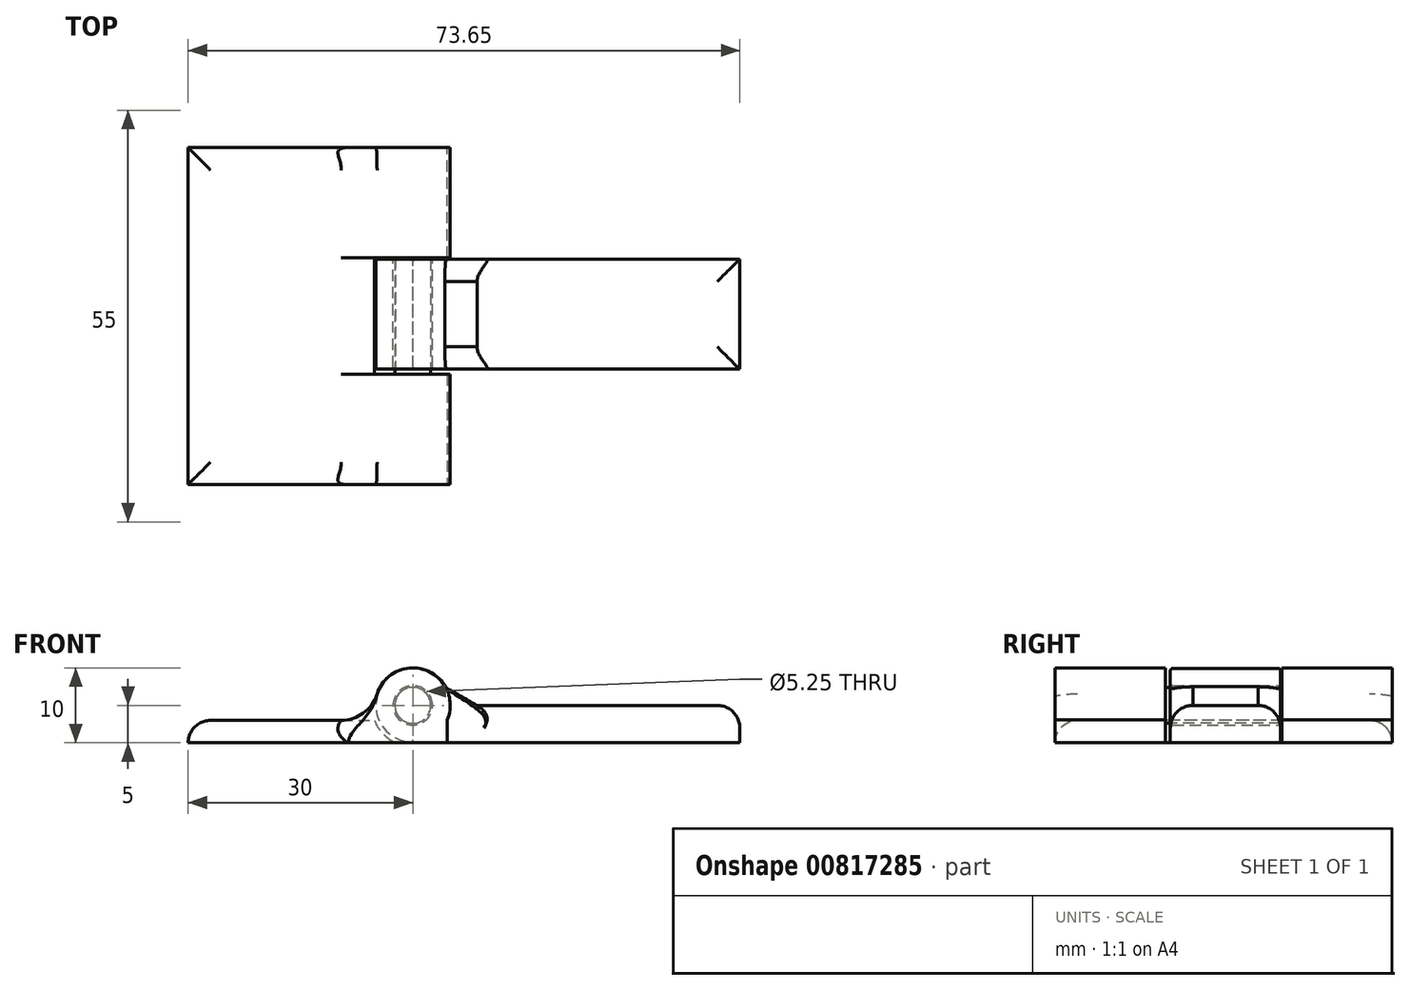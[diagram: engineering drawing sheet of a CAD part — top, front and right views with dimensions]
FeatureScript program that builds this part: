
annotation { "Feature Type Name" : "Feature", "Feature Type Description" : "" }
export const myFeature = defineFeature(function(context is Context, id is Id, definition is map)
    precondition{}
    {
        {
            var Q0;
            Q0=qCreatedBy(makeId("Top.planeOp"),FACE);
            var sketch = newSketch(context, id + "F0", { "sketchPlane" : qUnion([Q0])});
            skLineSegment(sketch, "E0.bottom", {"start": v(0, 0) * mm, "end": v(-30, 0) * mm});
            skLineSegment(sketch, "E0.top", {"start": v(0, -45) * mm, "end": v(-30, -45) * mm});
            skLineSegment(sketch, "E0.left", {"start": v(0, 0) * mm, "end": v(0, -45) * mm});
            skLineSegment(sketch, "E0.right", {"start": v(-30, 0) * mm, "end": v(-30, -45) * mm});
            skSolve(sketch);
        }
        {
            var Q0;
            Q0 = qSketchRegion(id + "F0", true);
            extrude(context, id + "F1", {"entities" : qUnion([Q0]), "depth" : 3 * mm, "offsetDistance" : 25 * mm});
        }
        {
            var Q0;
            Q0=makeQuery(id+"F1.opExtrude","SWEPT_FACE",FACE,{"disambiguationData":[OSD([sQuery(id+"F0.wireOp",EDGE,"E0.top")])]});
            var sketch = newSketch(context, id + "F2", { "sketchPlane" : qUnion([Q0])});
            skCircle(sketch, "E1", {"center": v(0, 5) * mm, "radius": 5 * mm});
            skLineSegment(sketch, "E2.bottom", {"start": v(0, 0) * mm, "end": v(4.6, 0) * mm});
            skLineSegment(sketch, "E2.top", {"start": v(0, 3.04) * mm, "end": v(4.6, 3.04) * mm});
            skLineSegment(sketch, "E2.left", {"start": v(0, 0) * mm, "end": v(0, 3.04) * mm});
            skLineSegment(sketch, "E2.right", {"start": v(4.6, 0) * mm, "end": v(4.6, 3.04) * mm});
            skSolve(sketch);
        }
        {
            var Q0;
            Q0 = qSketchRegion(id + "F2", true);
            extrude(context, id + "F3", {"entities" : qUnion([Q0]), "operationType" : NewBodyOperationType.ADD, "oppositeDirection" : true, "depth" : 14.7 * mm, "offsetDistance" : 25 * mm});
        }
        {
            var Q0;
            Q0=makeQuery(id+"F1.opExtrude","SWEPT_FACE",FACE,{"disambiguationData":[OSD([sQuery(id+"F0.wireOp",EDGE,"E0.bottom")])]});
            var sketch = newSketch(context, id + "F4", { "sketchPlane" : qUnion([Q0])});
            skCircle(sketch, "E3", {"center": v(0, 5) * mm, "radius": 5 * mm});
            skLineSegment(sketch, "E4.bottom", {"start": v(0, 0) * mm, "end": v(-4.6, 0) * mm});
            skLineSegment(sketch, "E4.top", {"start": v(0, 3.04) * mm, "end": v(-4.6, 3.04) * mm});
            skLineSegment(sketch, "E4.left", {"start": v(0, 0) * mm, "end": v(0, 3.04) * mm});
            skLineSegment(sketch, "E4.right", {"start": v(-4.6, 0) * mm, "end": v(-4.6, 3.04) * mm});
            skSolve(sketch);
        }
        {
            var Q0;
            Q0 = qSketchRegion(id + "F4", true);
            extrude(context, id + "F5", {"entities" : qUnion([Q0]), "operationType" : NewBodyOperationType.ADD, "oppositeDirection" : true, "depth" : 14.7 * mm, "offsetDistance" : 25 * mm});
        }
        {
            var Q0;
            Q0=makeQuery(id+"F3.opExtrude","CAP_FACE",FACE,{"disambiguationData":[OSD([sQuery(id+"F2.wireOp",EDGE,"E1")])],"isStart":false});
            var sketch = newSketch(context, id + "F6", { "sketchPlane" : qUnion([Q0])});
            skCircle(sketch, "E5", {"center": v(0, 5) * mm, "radius": 5.5 * mm});
            skSolve(sketch);
        }
        {
            var Q0;
            Q0 = qSketchRegion(id + "F6", true);
            var Q1;
            Q1=makeQuery(id+"F5.opExtrude","CAP_FACE",FACE,{"disambiguationData":[OSD([sQuery(id+"F4.wireOp",EDGE,"E3")])],"isStart":false});
            extrude(context, id + "F7", {"entities" : qUnion([Q0]), "operationType" : NewBodyOperationType.REMOVE, "endBound" : BoundingType.UP_TO_SURFACE, "depth" : 25 * mm, "endBoundEntityFace" : qUnion([Q1]), "offsetDistance" : 25 * mm});
        }
        {
            var Q0;
            Q0=makeQuery(id+"F3.boolean.opBoolean","MERGE",FACE,{"derivedFrom":[makeQuery(id+"F1.opExtrude","SWEPT_FACE",FACE,{"disambiguationData":[OSD([sQuery(id+"F0.wireOp",EDGE,"E0.top")])]}),makeQuery(id+"F3.opExtrude","CAP_FACE",FACE,{"disambiguationData":[OSD([sQuery(id+"F2.wireOp",EDGE,"E1")])],"isStart":true})]});
            var sketch = newSketch(context, id + "F8", { "sketchPlane" : qUnion([Q0])});
            skCircle(sketch, "E6", {"center": v(0, 5) * mm, "radius": 2.4 * mm});
            skSolve(sketch);
        }
        {
            var Q0;
            Q0 = qSketchRegion(id + "F8", true);
            var Q1;
            Q1=makeQuery(id+"F5.opExtrude","CAP_FACE",FACE,{"disambiguationData":[OSD([sQuery(id+"F4.wireOp",EDGE,"E3")])],"isStart":false});
            extrude(context, id + "F9", {"entities" : qUnion([Q0]), "operationType" : NewBodyOperationType.ADD, "endBound" : BoundingType.UP_TO_SURFACE, "oppositeDirection" : true, "depth" : 25 * mm, "endBoundEntityFace" : qUnion([Q1]), "offsetDistance" : 25 * mm});
        }
        {
            var Q0;
            {var subQ0=sQuery(id+"F4.wireOp",EDGE,"E4.right");var subQ1=sQuery(id+"F4.wireOp",EDGE,"E4.bottom");var subQ2=sQuery(id+"F4.wireOp",EDGE,"E3");Q0=makeQuery(id+"F7.boolean.opBoolean","MERGE",FACE,{"derivedFrom":[makeQuery(id+"F5.opExtrude","CAP_FACE",FACE,{"disambiguationData":[OSD([subQ2,subQ1,subQ0])],"isStart":false}),makeQuery(id+"F7.opExtrude","CAP_FACE",FACE,{"disambiguationData":[OSD([subQ2,subQ1,subQ0])],"isStart":false})]});}
            cPlane(context, id + "F10", {"entities" : qUnion([Q0]), "cplaneType" : CPlaneType.OFFSET, "offset" : .2 * mm, "width" : 150 * mm, "height" : 150 * mm});
        }
        {
            var Q0;
            Q0=qCreatedBy(id+"F10.planeOp",FACE);
            var sketch = newSketch(context, id + "F11", { "sketchPlane" : qUnion([Q0])});
            skCircle(sketch, "E7", {"center": v(0, 5) * mm, "radius": 2.62 * mm});
            skCircle(sketch, "E8", {"center": v(0, 5) * mm, "radius": 4.92 * mm});
            skLineSegment(sketch, "E9.bottom", {"start": v(3.65, 5) * mm, "end": v(43.65, 5) * mm});
            skLineSegment(sketch, "E9.top", {"start": v(3.65, 0) * mm, "end": v(43.65, 0) * mm});
            skLineSegment(sketch, "E9.left", {"start": v(3.65, 5) * mm, "end": v(3.65, 0) * mm});
            skLineSegment(sketch, "E9.right", {"start": v(43.65, 5) * mm, "end": v(43.65, 0) * mm});
            skLineSegment(sketch, "E10.bottom", {"start": v(3.65, 0) * mm, "end": v(0, 0) * mm});
            skLineSegment(sketch, "E10.top", {"start": v(3.65, 2.38) * mm, "end": v(0, 2.38) * mm});
            skLineSegment(sketch, "E10.left", {"start": v(3.65, 0) * mm, "end": v(3.65, 2.38) * mm});
            skLineSegment(sketch, "E10.right", {"start": v(0, 0) * mm, "end": v(0, 2.38) * mm});
            skSolve(sketch);
        }
        {
            var Q0;
            Q0 = qSketchRegion(id + "F11", true);
            extrude(context, id + "F12", {"entities" : qUnion([Q0]), "depth" : 14.7 * mm, "offsetDistance" : 25 * mm});
        }
        {
            var Q0;
            Q0=makeQuery(id+"F1.opExtrude","CAP_EDGE",EDGE,{"disambiguationData":[OSD([sQuery(id+"F0.wireOp",EDGE,"E0.bottom")])],"isStart":false});
            var Q1;
            Q1=makeQuery(id+"F1.opExtrude","CAP_EDGE",EDGE,{"disambiguationData":[OSD([sQuery(id+"F0.wireOp",EDGE,"E0.right")])],"isStart":false});
            var Q2;
            Q2=makeQuery(id+"F1.opExtrude","CAP_EDGE",EDGE,{"disambiguationData":[OSD([sQuery(id+"F0.wireOp",EDGE,"E0.top")])],"isStart":false});
            var Q3;
            Q3=makeQuery(id+"F12.opExtrude","CAP_EDGE",EDGE,{"disambiguationData":[OSD([sQuery(id+"F11.wireOp",EDGE,"E9.bottom")])],"isStart":false});
            var Q4;
            Q4=makeQuery(id+"F12.opExtrude","CAP_EDGE",EDGE,{"disambiguationData":[OSD([sQuery(id+"F11.wireOp",EDGE,"E9.bottom")])],"isStart":true});
            var Q5;
            Q5=makeQuery(id+"F12.opExtrude","SWEPT_EDGE",EDGE,{"disambiguationData":[OSD([sQuery(id+"F11.wireOp",EDGE,"E9.bottom"),sQuery(id+"F11.wireOp",EDGE,"E9.right")])]});
            fillet(context, id + "F13", {"entities" : qUnion([Q0, Q1, Q2, Q3, Q4, Q5]), "radius" : 3 * mm, "tangentPropagation" : true, "allowEdgeOverflow" : false});
        }
        {
            var Q0;
            Q0=makeQuery(id+"F12.opExtrude","SWEPT_EDGE",EDGE,{"disambiguationData":[OSD([sQuery(id+"F11.wireOp",EDGE,"E8"),sQuery(id+"F11.wireOp",EDGE,"E9.bottom")])]});
            chamfer(context, id + "F14", {"entities" : qUnion([Q0]), "width" : 5 * mm, "tangentPropagation" : true});
        }
        {
            var Q0;
            Q0=makeQuery(id+"F12.opExtrude","CAP_EDGE",EDGE,{"disambiguationData":[OSD([sQuery(id+"F11.wireOp",EDGE,"E7")])],"isStart":true});
            var Q1;
            {var subQ0=sQuery(id+"F4.wireOp",EDGE,"E4.right");var subQ1=sQuery(id+"F4.wireOp",EDGE,"E4.bottom");var subQ2=sQuery(id+"F4.wireOp",EDGE,"E3");Q1=makeQuery(id+"F9.opExtrude","TWEAK_EDGE",EDGE,{"derivedFrom":[makeQuery(id+"F7.boolean.opBoolean","MERGE",FACE,{"derivedFrom":[makeQuery(id+"F5.opExtrude","CAP_FACE",FACE,{"disambiguationData":[OSD([subQ2,subQ1,subQ0])],"isStart":false}),makeQuery(id+"F7.opExtrude","CAP_FACE",FACE,{"disambiguationData":[OSD([subQ2,subQ1,subQ0])],"isStart":false})]}),makeQuery(id+"F8.imprint","IMPRINT",EDGE,{"derivedFrom":sQuery(id+"F8.wireOp",EDGE,"E6")})]});}
            var Q2;
            Q2=makeQuery(id+"F12.opExtrude","CAP_EDGE",EDGE,{"disambiguationData":[OSD([sQuery(id+"F11.wireOp",EDGE,"E8")])],"isStart":true});
            var Q3;
            Q3=makeQuery(id+"F12.opExtrude","CAP_EDGE",EDGE,{"disambiguationData":[OSD([sQuery(id+"F11.wireOp",EDGE,"E8")])],"isStart":false});
            var Q4;
            Q4=makeQuery(id+"F9.boolean.opBoolean","INTERSECT",EDGE,{"derivedFrom":[makeQuery(id+"F7.boolean.opBoolean","MERGE",FACE,{"derivedFrom":[makeQuery(id+"F3.opExtrude","CAP_FACE",FACE,{"disambiguationData":[OSD([sQuery(id+"F2.wireOp",EDGE,"E1"),sQuery(id+"F2.wireOp",EDGE,"E2.bottom"),sQuery(id+"F2.wireOp",EDGE,"E2.right")])],"isStart":false}),makeQuery(id+"F7.opExtrude","CAP_FACE",FACE,{"disambiguationData":[OSD([sQuery(id+"F6.wireOp",EDGE,"E5")])],"isStart":true})]}),makeQuery(id+"F9.opExtrude","SWEPT_FACE",FACE,{"disambiguationData":[OSD([sQuery(id+"F8.wireOp",EDGE,"E6")])]})]});
            var Q5;
            Q5=makeQuery(id+"F12.opExtrude","CAP_EDGE",EDGE,{"disambiguationData":[OSD([sQuery(id+"F11.wireOp",EDGE,"E7")])],"isStart":false});
            fillet(context, id + "F15", {"entities" : qUnion([Q0, Q1, Q2, Q3, Q4, Q5]), "radius" : .3 * mm, "tangentPropagation" : true, "allowEdgeOverflow" : false});
        }
        {
            var Q0;
            Q0=makeQuery(id+"F5.boolean.opBoolean","INTERSECT",EDGE,{"derivedFrom":[makeQuery(id+"F1.opExtrude","CAP_FACE",FACE,{"disambiguationData":[OSD([sQuery(id+"F0.wireOp",EDGE,"E0.bottom"),sQuery(id+"F0.wireOp",EDGE,"E0.top"),sQuery(id+"F0.wireOp",EDGE,"E0.left"),sQuery(id+"F0.wireOp",EDGE,"E0.right")])],"isStart":false}),makeQuery(id+"F5.opExtrude","SWEPT_FACE",FACE,{"disambiguationData":[OSD([sQuery(id+"F4.wireOp",EDGE,"E3")])]})]});
            var Q1;
            Q1=makeQuery(id+"F3.boolean.opBoolean","INTERSECT",EDGE,{"derivedFrom":[makeQuery(id+"F1.opExtrude","CAP_FACE",FACE,{"disambiguationData":[OSD([sQuery(id+"F0.wireOp",EDGE,"E0.bottom"),sQuery(id+"F0.wireOp",EDGE,"E0.top"),sQuery(id+"F0.wireOp",EDGE,"E0.left"),sQuery(id+"F0.wireOp",EDGE,"E0.right")])],"isStart":false}),makeQuery(id+"F3.opExtrude","SWEPT_FACE",FACE,{"disambiguationData":[OSD([sQuery(id+"F2.wireOp",EDGE,"E1")])]})]});
            fillet(context, id + "F16", {"entities" : qUnion([Q0, Q1]), "radius" : 5 * mm, "tangentPropagation" : true, "allowEdgeOverflow" : false});
        }
    });
